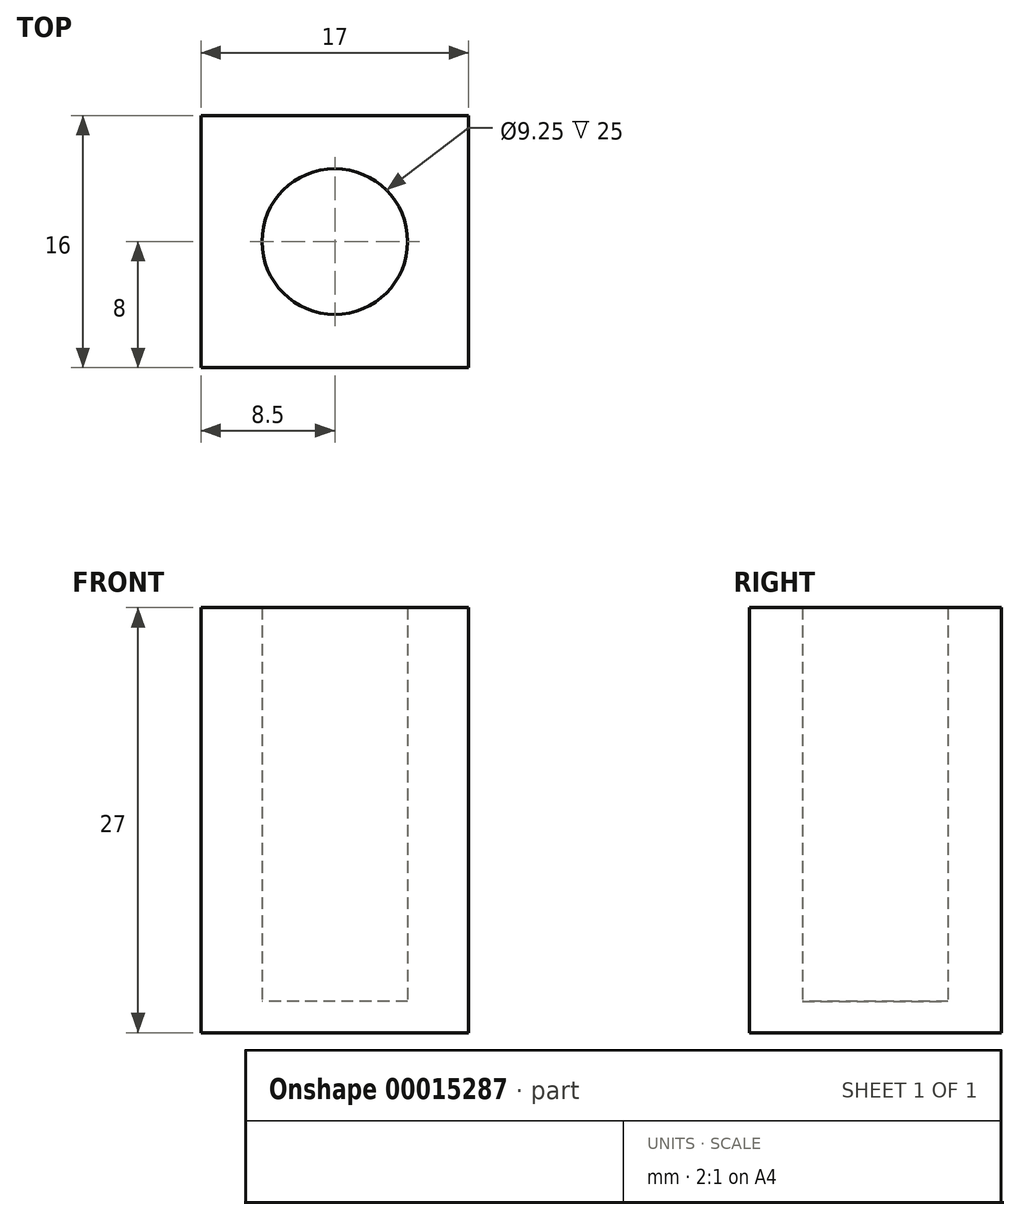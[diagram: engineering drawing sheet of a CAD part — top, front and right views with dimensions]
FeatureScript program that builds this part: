
annotation { "Feature Type Name" : "Feature", "Feature Type Description" : "" }
export const myFeature = defineFeature(function(context is Context, id is Id, definition is map)
    precondition{}
    {
        {
            var Q0;
            Q0=qCreatedBy(makeId("Top.planeOp"),FACE);
            var sketch = newSketch(context, id + "F0", { "sketchPlane" : qUnion([Q0])});
            skLineSegment(sketch, "E0.rect.bottom", {"start": v(-8.5, 8) * mm, "end": v(8.5, 8) * mm});
            skLineSegment(sketch, "E0.rect.top", {"start": v(-8.5, -8) * mm, "end": v(8.5, -8) * mm});
            skLineSegment(sketch, "E0.rect.left", {"start": v(-8.5, 8) * mm, "end": v(-8.5, -8) * mm});
            skLineSegment(sketch, "E0.rect.right", {"start": v(8.5, 8) * mm, "end": v(8.5, -8) * mm});
            skPoint(sketch, "E0.rect.middle", {"position": v(0, 0) * mm});
            skCircle(sketch, "E1", {"center": v(0, 0) * mm, "radius": 4.62 * mm});
            skSolve(sketch);
        }
        {
            var Q0;
            Q0 = qSketchRegion(id + "F0", true);
            var Q1;
            Q1=makeQuery(id+"F0.imprint","IMPRINT",FACE,{"disambiguationData":[TD([[makeQuery(id+"F0.imprint","IMPRINT",EDGE,{"derivedFrom":sQuery(id+"F0.wireOp",EDGE,"E1")}),1.0]])]});
            extrude(context, id + "F1", {"entities" : qUnion([Q0, Q1]), "oppositeDirection" : true, "depth" : 2 * mm});
        }
        {
            var Q0;
            Q0 = qSketchRegion(id + "F0", true);
            extrude(context, id + "F2", {"entities" : qUnion([Q0]), "operationType" : NewBodyOperationType.ADD, "depth" : 25 * mm});
        }
    });
